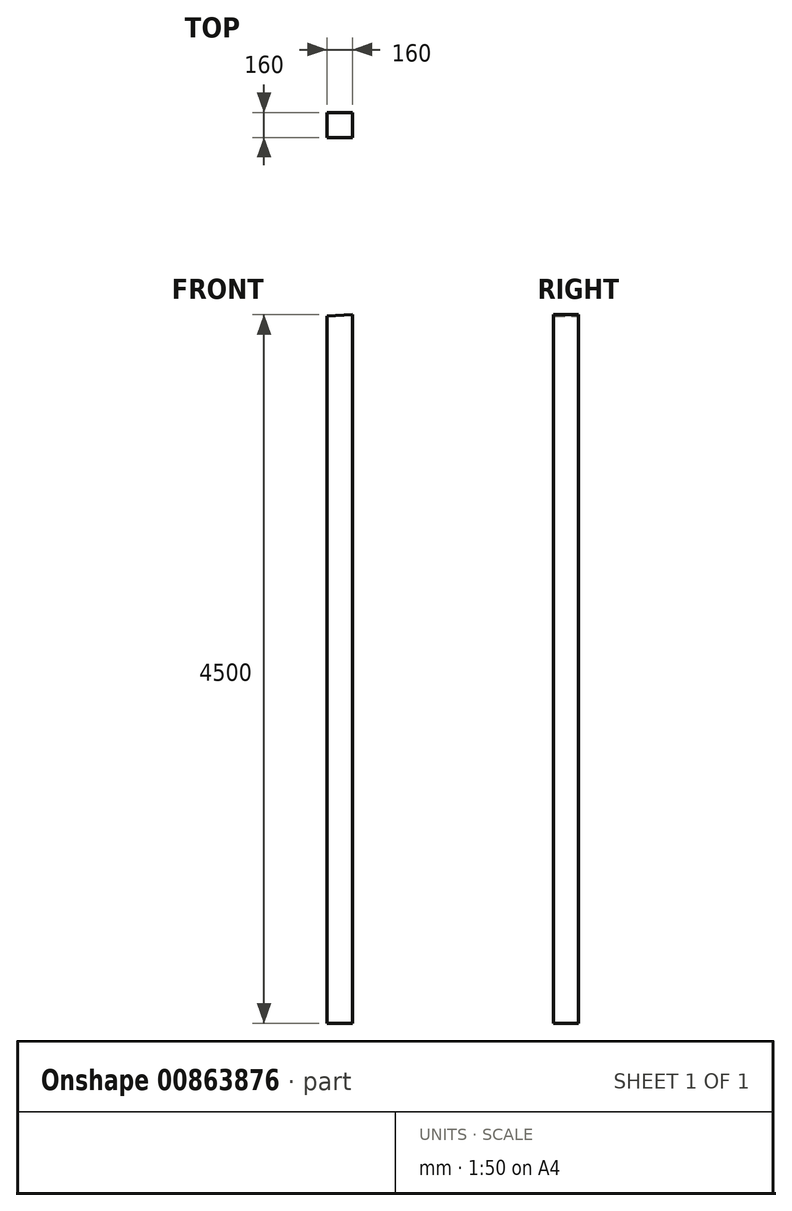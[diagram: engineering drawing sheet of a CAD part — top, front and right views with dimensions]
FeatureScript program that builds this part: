
annotation { "Feature Type Name" : "Feature", "Feature Type Description" : "" }
export const myFeature = defineFeature(function(context is Context, id is Id, definition is map)
    precondition{}
    {
        {
            var Q0;
            Q0=qCreatedBy(makeId("Front.planeOp"),FACE);
            var sketch = newSketch(context, id + "F0", { "sketchPlane" : qUnion([Q0])});
            skLineSegment(sketch, "E0", {"start": v(-485.61, -2262.72) * mm, "end": v(-485.61, 2228.9) * mm});
            skLineSegment(sketch, "E1", {"start": v(-325.61, 2237.28) * mm, "end": v(-485.61, 2228.9) * mm});
            skLineSegment(sketch, "E2", {"start": v(-325.61, 2237.28) * mm, "end": v(-325.61, -2262.72) * mm});
            skLineSegment(sketch, "E3", {"start": v(-325.61, -2262.72) * mm, "end": v(-485.61, -2262.72) * mm});
            skSolve(sketch);
        }
        {
            var Q0;
            Q0=makeQuery(id+"F0.imprint","IMPRINT",FACE,{"disambiguationData":[TD([[makeQuery(id+"F0.imprint","IMPRINT",EDGE,{"derivedFrom":sQuery(id+"F0.wireOp",EDGE,"E0")}),-1.0]])]});
            extrude(context, id + "F1", {"entities" : qUnion([Q0]), "endBound" : BoundingType.SYMMETRIC, "depth" : 160 * mm, "offsetDistance" : 25 * mm});
        }
    });
